# Revit family: UM397S Silla Leman
name_source: partatom
category: Mobiliario
units: mm (PartAtom-declared; Revit-internal decimal feet)

## family parameters
Compartido = No
Corte con vacíos al cargar = No
Número OmniClass = 23.40.20.00
Punto de cálculo de habitación = No
Se basa en plano de trabajo = No
Siempre vertical = Sí
Título OmniClass = General Furniture and Specialties

## types (1)
- UM397S Silla Leman
    Acabado Listones = Lignus, protector fungicida, insecticida e hidrófugo.
    Acabado bancada = Ferrus, proceso protector del hierro.Acabado imprimación epoxi y pintura poliéster en polvo color gris.
    Accessibilidad = Sí
    Altura asiento = 420 mm  [stored 1.37795 ft]
    Altura total = 830 mm  [stored 2.7231 ft]
    Ancho = 600 mm
    Comentarios de tipo = Pies de fundición dúctil, con tratamiento Ferrus, proceso protector del hierro que garantiza una óptima resistencia a la corrosión. Acabado imprimación epoxi y pintura poliéster en polvo color gris. Tablones de sección 55 x 30 mm de madera tropical tratada con Lignus, protector fungicida, insecticida e hidrófugo. Acabado color caoba. Tornillos de acero inoxidable.
    Fabricante = BENITO
    Ficha tecnica = http://www.benito.com
    Instalación = Anclaje recomendado: Tornillos de fijación al suelo de M10 según superficie y proyecto.
    Largo = 650 mm  [stored 2.13255 ft]
    Material bancada = Fundición dúctil
    Material listones = Madera Tropical
    Modelo = Silla Leman
    Referencia = UM397S
    URL = http://www.benito.com
    URL Producto = http://www.benito.com

note: [stored X ft] marks values corroborated as IEEE doubles in the binary element streams (Revit-internal decimal feet)

## geometry (parser evidence)
native form markers: Blend x4
no freeform markers — native parametric forms only
